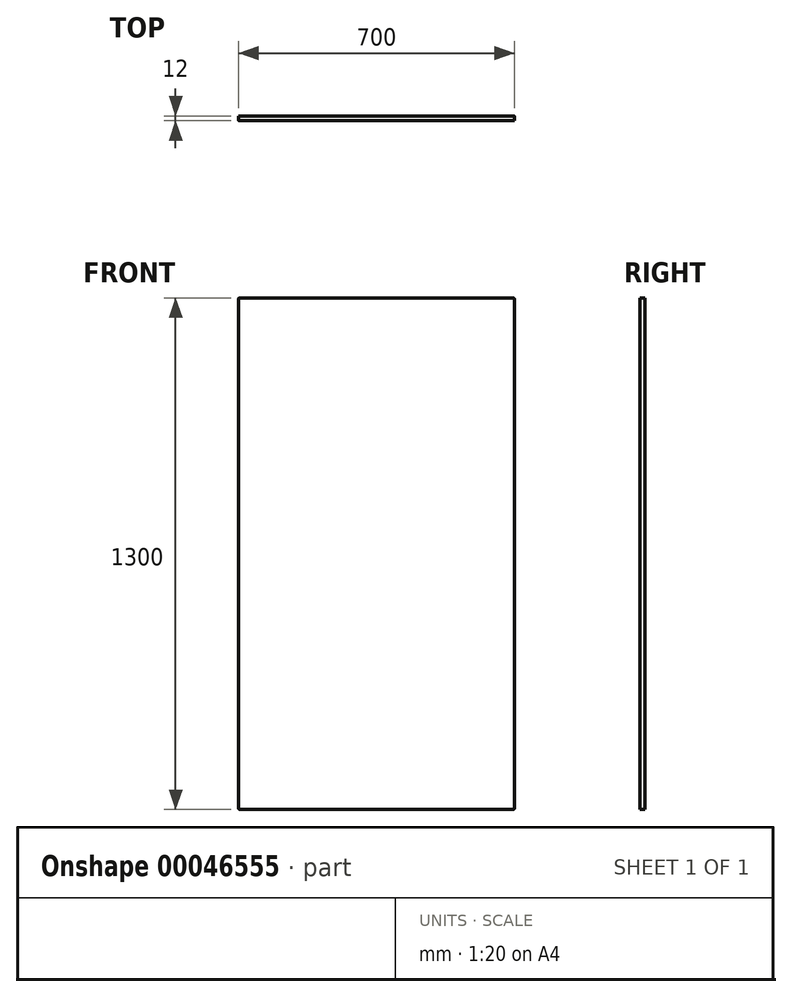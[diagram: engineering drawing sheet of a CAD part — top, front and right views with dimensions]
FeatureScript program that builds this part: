
annotation { "Feature Type Name" : "Feature", "Feature Type Description" : "" }
export const myFeature = defineFeature(function(context is Context, id is Id, definition is map)
    precondition{}
    {
        {
            var Q0;
            Q0=qCreatedBy(makeId("Front.planeOp"),FACE);
            var sketch = newSketch(context, id + "F0", { "sketchPlane" : qUnion([Q0])});
            skLineSegment(sketch, "E0.bottom", {"start": v(-39.3, 1253.82) * mm, "end": v(660.7, 1253.82) * mm});
            skLineSegment(sketch, "E0.top", {"start": v(-39.3, -46.18) * mm, "end": v(660.7, -46.18) * mm});
            skLineSegment(sketch, "E0.left", {"start": v(-39.3, 1253.82) * mm, "end": v(-39.3, -46.18) * mm});
            skLineSegment(sketch, "E0.right", {"start": v(660.7, 1253.82) * mm, "end": v(660.7, -46.18) * mm});
            skSolve(sketch);
        }
        {
            var Q0;
            Q0=makeQuery(id+"F0.imprint","IMPRINT",FACE,{"disambiguationData":[TD([[makeQuery(id+"F0.imprint","IMPRINT",EDGE,{"derivedFrom":sQuery(id+"F0.wireOp",EDGE,"E0.bottom")}),-1.0]])]});
            extrude(context, id + "F1", {"entities" : qUnion([Q0]), "depth" : 12 * mm});
        }
        {
            var Q0;
            Q0=makeQuery(id+"F1.opExtrude","SWEPT_EDGE",EDGE,{"disambiguationData":[OSD([sQuery(id+"F0.wireOp",EDGE,"E0.bottom"),sQuery(id+"F0.wireOp",EDGE,"E0.right")])]});
            var Q1;
            Q1=makeQuery(id+"F1.opExtrude","SWEPT_EDGE",EDGE,{"disambiguationData":[OSD([sQuery(id+"F0.wireOp",EDGE,"E0.bottom"),sQuery(id+"F0.wireOp",EDGE,"E0.left")])]});
            var Q2;
            Q2=makeQuery(id+"F1.opExtrude","SWEPT_EDGE",EDGE,{"disambiguationData":[OSD([sQuery(id+"F0.wireOp",EDGE,"E0.top"),sQuery(id+"F0.wireOp",EDGE,"E0.left")])]});
            var Q3;
            Q3=makeQuery(id+"F1.opExtrude","SWEPT_EDGE",EDGE,{"disambiguationData":[OSD([sQuery(id+"F0.wireOp",EDGE,"E0.top"),sQuery(id+"F0.wireOp",EDGE,"E0.right")])]});
            fillet(context, id + "F2", {"entities" : qUnion([Q0, Q1, Q2, Q3]), "radius" : 2 * mm, "tangentPropagation" : true, "allowEdgeOverflow" : false});
        }
    });
